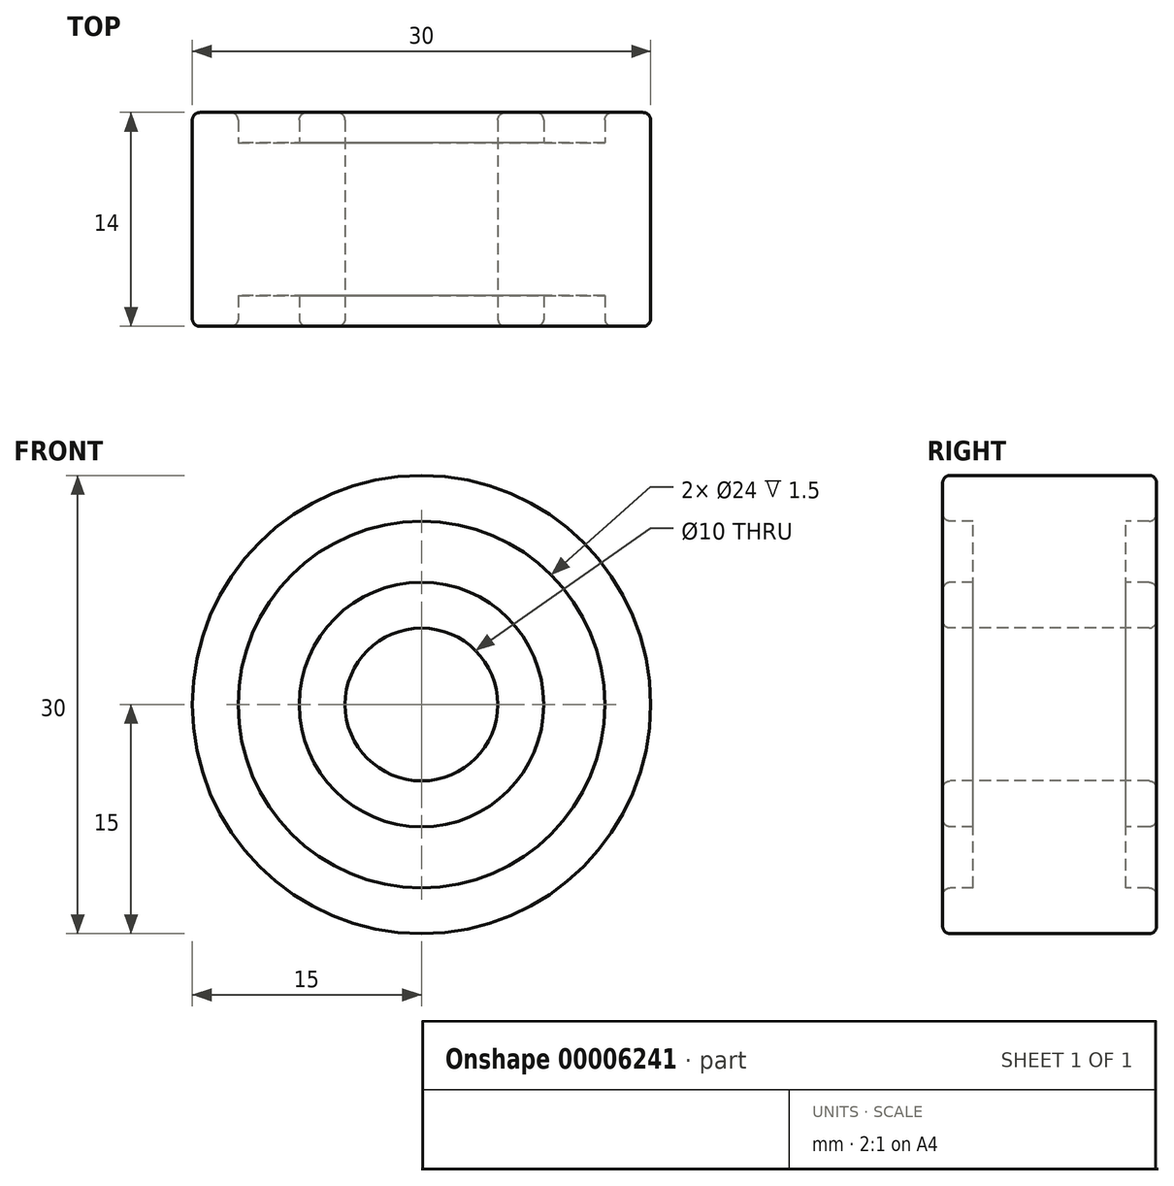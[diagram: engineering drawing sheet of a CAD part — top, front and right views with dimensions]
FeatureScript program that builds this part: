
annotation { "Feature Type Name" : "Feature", "Feature Type Description" : "" }
export const myFeature = defineFeature(function(context is Context, id is Id, definition is map)
    precondition{}
    {
        {
            var Q0;
            Q0=qCreatedBy(makeId("Right.planeOp"),FACE);
            var sketch = newSketch(context, id + "F0", { "sketchPlane" : qUnion([Q0])});
            skLineSegment(sketch, "E0.bottom", {"start": v(0, 5) * mm, "end": v(14, 5) * mm});
            skLineSegment(sketch, "E0.top", {"start": v(0, 15) * mm, "end": v(14, 15) * mm});
            skLineSegment(sketch, "E0.left", {"start": v(0, 5) * mm, "end": v(0, 8) * mm});
            skLineSegment(sketch, "E0.right", {"start": v(14, 5) * mm, "end": v(14, 8) * mm});
            skLineSegment(sketch, "E1", {"start": v(0, 12) * mm, "end": v(2, 12) * mm});
            skLineSegment(sketch, "E2", {"start": v(2, 12) * mm, "end": v(2, 8) * mm});
            skLineSegment(sketch, "E3", {"start": v(2, 8) * mm, "end": v(0, 8) * mm});
            skLineSegment(sketch, "E4", {"start": v(14, 12) * mm, "end": v(12, 12) * mm});
            skLineSegment(sketch, "E5", {"start": v(12, 12) * mm, "end": v(12, 8) * mm});
            skLineSegment(sketch, "E6", {"start": v(12, 8) * mm, "end": v(14, 8) * mm});
            skLineSegment(sketch, "E7.trimOffspring", {"start": v(0, 12) * mm, "end": v(0, 15) * mm});
            skLineSegment(sketch, "E8.trimOffspring", {"start": v(14, 12) * mm, "end": v(14, 15) * mm});
            skLineSegment(sketch, "E9", {"start": v(-33.64, 0) * mm, "end": v(52.62, 0) * mm, "construction": true});
            skSolve(sketch);
        }
        {
            var Q0;
            Q0=makeQuery(id+"F0.imprint","IMPRINT",FACE,{"disambiguationData":[TD([[makeQuery(id+"F0.imprint","IMPRINT",EDGE,{"derivedFrom":sQuery(id+"F0.wireOp",EDGE,"E0.bottom")}),1.0]])]});
            var Q1;
            Q1=sQuery(id+"F0.wireOp",EDGE,"E9");
            revolve(context, id + "F1", {"entities" : qUnion([Q0]), "axis" : qUnion([Q1]), "revolveType" : RevolveType.FULL});
        }
        {
            var Q0;
            Q0=makeQuery(id+"F1.opRevolve","SWEPT_EDGE",EDGE,{"disambiguationData":[OSD([sQuery(id+"F0.wireOp",EDGE,"E0.top"),sQuery(id+"F0.wireOp",EDGE,"E7.trimOffspring")])]});
            var Q1;
            Q1=makeQuery(id+"F1.opRevolve","SWEPT_EDGE",EDGE,{"disambiguationData":[OSD([sQuery(id+"F0.wireOp",EDGE,"E0.top"),sQuery(id+"F0.wireOp",EDGE,"E8.trimOffspring")])]});
            var Q2;
            Q2=makeQuery(id+"F1.opRevolve","SWEPT_EDGE",EDGE,{"disambiguationData":[OSD([sQuery(id+"F0.wireOp",EDGE,"E0.bottom"),sQuery(id+"F0.wireOp",EDGE,"E0.left")])]});
            var Q3;
            Q3=makeQuery(id+"F1.opRevolve","SWEPT_EDGE",EDGE,{"disambiguationData":[OSD([sQuery(id+"F0.wireOp",EDGE,"E0.bottom"),sQuery(id+"F0.wireOp",EDGE,"E0.right")])]});
            var Q4;
            Q4=makeQuery(id+"F1.opRevolve","SWEPT_EDGE",EDGE,{"disambiguationData":[OSD([sQuery(id+"F0.wireOp",EDGE,"E4"),sQuery(id+"F0.wireOp",EDGE,"E8.trimOffspring")])]});
            var Q5;
            Q5=makeQuery(id+"F1.opRevolve","SWEPT_EDGE",EDGE,{"disambiguationData":[OSD([sQuery(id+"F0.wireOp",EDGE,"E0.right"),sQuery(id+"F0.wireOp",EDGE,"E6")])]});
            var Q6;
            Q6=makeQuery(id+"F1.opRevolve","SWEPT_EDGE",EDGE,{"disambiguationData":[OSD([sQuery(id+"F0.wireOp",EDGE,"E0.left"),sQuery(id+"F0.wireOp",EDGE,"E3")])]});
            var Q7;
            Q7=makeQuery(id+"F1.opRevolve","SWEPT_EDGE",EDGE,{"disambiguationData":[OSD([sQuery(id+"F0.wireOp",EDGE,"E1"),sQuery(id+"F0.wireOp",EDGE,"E7.trimOffspring")])]});
            fillet(context, id + "F2", {"entities" : qUnion([Q0, Q1, Q2, Q3, Q4, Q5, Q6, Q7]), "radius" : .5 * mm, "tangentPropagation" : true, "allowEdgeOverflow" : false});
        }
    });
